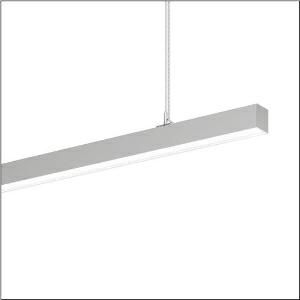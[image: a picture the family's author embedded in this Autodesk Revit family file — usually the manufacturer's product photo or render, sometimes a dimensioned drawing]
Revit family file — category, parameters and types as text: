
# Revit family: silica_r__21_51mx33db49sb_c15f
name_source: partatom
category: Lighting Fixtures
units: mm (PartAtom-declared; Revit-internal decimal feet)

## family parameters
Cut with Voids When Loaded = No
Host = Face
Light Source = No
Part Type = Normal
Room Calculation Point = No
Round Connector Dimension = Use Diameter
Shared = No

## types (1)
- --- (1 x LED, 7390 lm, 48.3 W, 4000K)
    Apparent Load = 48 VA
    CIE Flux Codes = 78 96 99 55 100
    Color Rendering = 80
    Color Temperature = 4000K
    Default Elevation = 1800 mm
    Description = Silica® 21, office luminaire, primary optical cover: prismatic diffuser, of PMMA, CAT 2 (L<= 3000cd/m²), light emission: direct/indirect distribution, primary light characteristic: symmetric, installation type: suspended mounting, LED, rated luminous flux: 7.390lm, luminous efficacy: 153lm/W, light colour: 840, colour temperature: 4000K, with terminal, 3+2-pole, max. 2.5mm², mains connection: 220..240V, AC, 50/60Hz, rated input power: 48.3W, luminaire housing, of aluminium, metallic grey (RAL 9006), length: 1.504mm, width: 53mm, height: 53mm, protection rating (complete): IP20, insulation class (complete): insulation class I (protective earthing), certification: CE, permissible operating ambient temperature: 0..+35°C, standard: EN 50419, packaging unit: 1 piece
    Height = 53 mm
    Lamp = 1 x LED
    Lamp Light Flux = 7390 lm
    Lamp Power = 48.3 W
    Lamp count = 1
    Length = 1504 mm
    Luminous efficacy = 153 lm/W
    Manufacturer = Siteco
    ModVariant = No
    Model = 51MX33DB49SB
    Mounting Place = Ceiling
    Mounting Type = Pendant
    Number of Poles = 1
    OnlyDefault = Yes
    Power Factor = 1
    Product Name = Silica® 21
    Product group = office luminaire | ceiling pendant
    ProductGroupID = 902
    Protection Class = Protection class I
    Protection Degree = IP 20
    RLX_Detail_Level = 1
    RLX_Emergency_Light_Flux = 0 lm
    RLX_Emergency_Type = 0
    RLX_Emergency_Type_DB = No
    RlxData = <blob elided: 23533 chars, md5=65660422>
    Socket = socket
    Standby Power = 0 W
    System Light Flux = 7390 lm
    System Power = 48 W
    Type Comments = factory setting: luminous flux: 100 % | dim-lin: 254 | 323 mA
    Type Image = l_1297747.jpg
    URL = http://relux.com
    VarID = @adj_048695
    Voltage = 0 V
    Weight = 0.00 kg
    Width = 53 mm

## geometry (parser evidence)
native form markers: Blend x4, Sweep x14
no freeform markers — native parametric forms only
